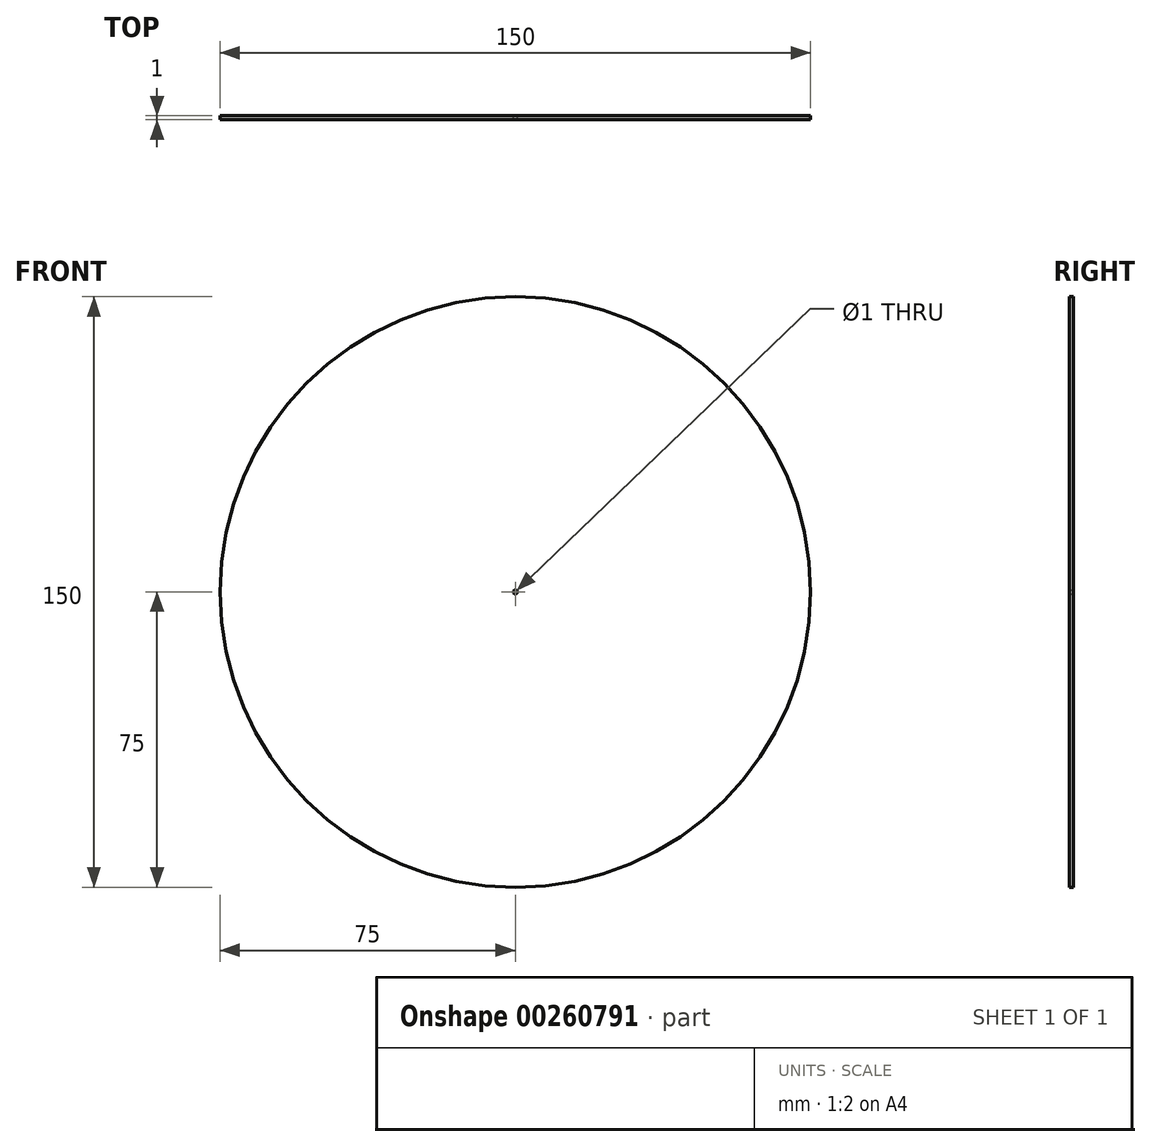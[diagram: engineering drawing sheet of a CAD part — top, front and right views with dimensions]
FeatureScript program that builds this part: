
annotation { "Feature Type Name" : "Feature", "Feature Type Description" : "" }
export const myFeature = defineFeature(function(context is Context, id is Id, definition is map)
    precondition{}
    {
        {
            var Q0;
            Q0=qCreatedBy(makeId("Front.planeOp"),FACE);
            var sketch = newSketch(context, id + "F0", { "sketchPlane" : qUnion([Q0])});
            skCircle(sketch, "E0", {"center": v(0, 0) * mm, "radius": 75 * mm});
            skCircle(sketch, "E1", {"center": v(0, 0) * mm, "radius": 0.5 * mm});
            skSolve(sketch);
        }
        {
            var Q0;
            Q0=makeQuery(id+"F0.imprint","IMPRINT",FACE,{"disambiguationData":[TD([[makeQuery(id+"F0.imprint","IMPRINT",EDGE,{"derivedFrom":sQuery(id+"F0.wireOp",EDGE,"E0")}),1.0]])]});
            extrude(context, id + "F1", {"entities" : qUnion([Q0]), "depth" : 1 * mm});
        }
    });
